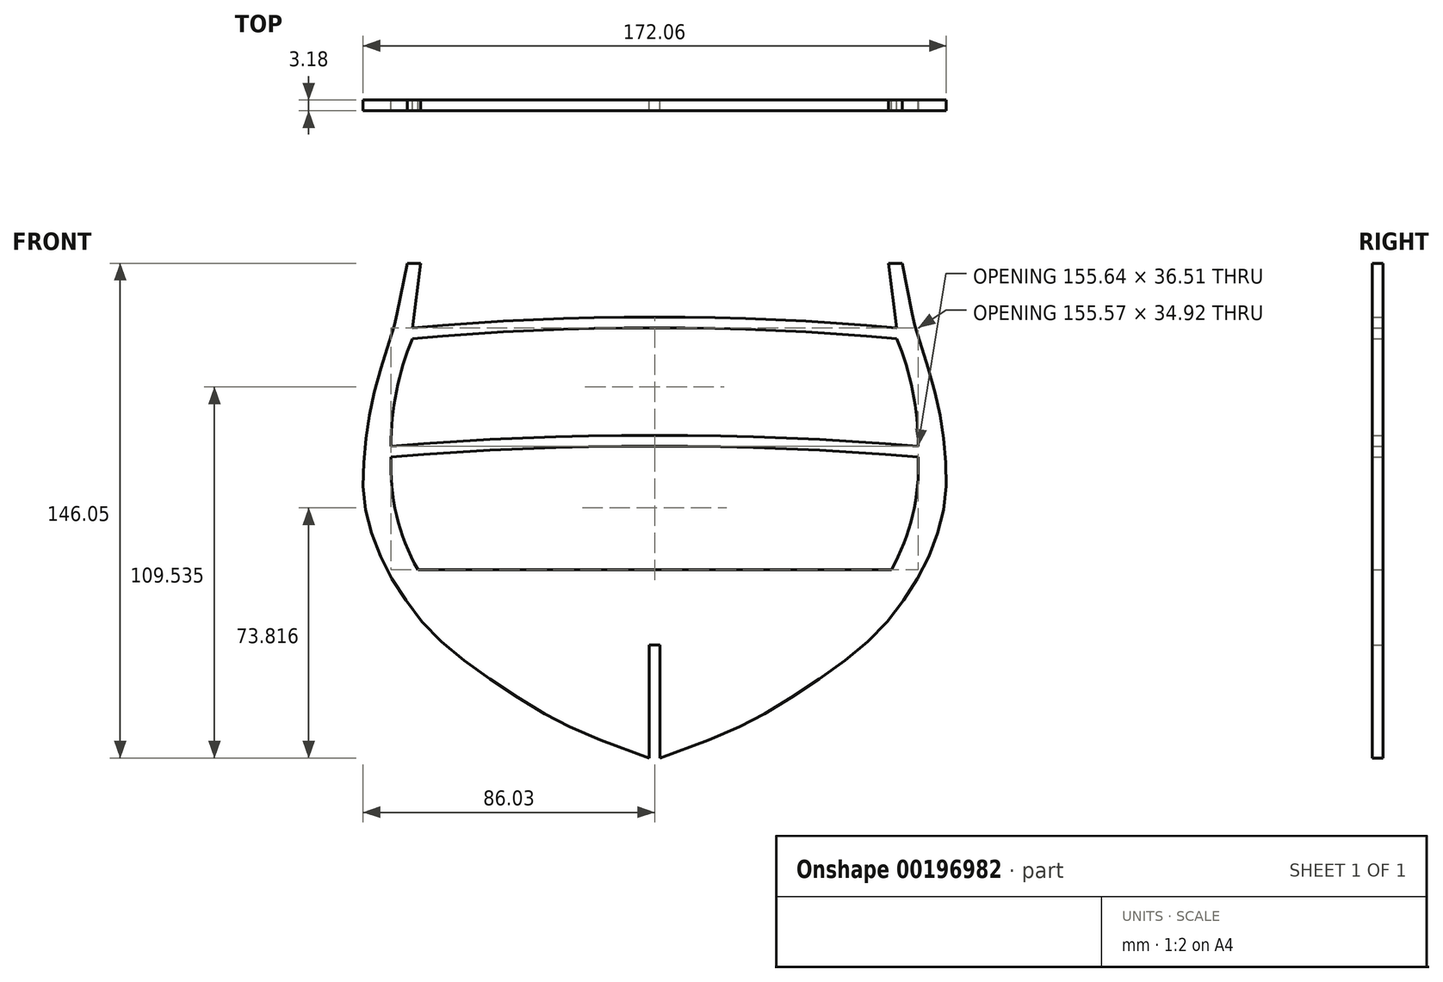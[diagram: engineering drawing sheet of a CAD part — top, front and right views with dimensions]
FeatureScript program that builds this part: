
annotation { "Feature Type Name" : "Feature", "Feature Type Description" : "" }
export const myFeature = defineFeature(function(context is Context, id is Id, definition is map)
    precondition{}
    {
        {
            var Q0;
            Q0=qCreatedBy(makeId("Front.planeOp"),FACE);
            var sketch = newSketch(context, id + "F0", { "sketchPlane" : qUnion([Q0])});
            skLineSegment(sketch, "E0", {"start": v(0, 0) * mm, "end": v(0, -22.22) * mm, "construction": true});
            skLineSegment(sketch, "E1", {"start": v(0, -22.22) * mm, "end": v(1.59, -22.22) * mm});
            skLineSegment(sketch, "E2", {"start": v(1.59, -22.22) * mm, "end": v(1.59, -55.56) * mm});
            skLineSegment(sketch, "E3", {"start": v(1.59, -55.56) * mm, "end": v(-1.59, -55.56) * mm, "construction": true});
            skLineSegment(sketch, "E4", {"start": v(-1.59, -55.56) * mm, "end": v(-1.59, -22.22) * mm});
            skLineSegment(sketch, "E5", {"start": v(-1.59, -22.22) * mm, "end": v(0, -22.22) * mm});
            skLineSegment(sketch, "E6", {"start": v(0, 0) * mm, "end": v(0, 33.34) * mm, "construction": true});
            skLineSegment(sketch, "E7", {"start": v(0, 33.34) * mm, "end": v(0, 36.51) * mm, "construction": true});
            skLineSegment(sketch, "E8", {"start": v(0, 36.51) * mm, "end": v(0, 68.26) * mm, "construction": true});
            skLineSegment(sketch, "E9", {"start": v(0, 68.26) * mm, "end": v(0, 71.44) * mm, "construction": true});
            skLineSegment(sketch, "E10", {"start": v(-71.44, 68.26) * mm, "end": v(0, 68.26) * mm, "construction": true});
            skLineSegment(sketch, "E11", {"start": v(0, 68.26) * mm, "end": v(71.44, 68.26) * mm, "construction": true});
            skLineSegment(sketch, "E12", {"start": v(0, 33.34) * mm, "end": v(77.79, 33.34) * mm, "construction": true});
            skLineSegment(sketch, "E13", {"start": v(0, 33.34) * mm, "end": v(-77.79, 33.34) * mm, "construction": true});
            skLineSegment(sketch, "E14", {"start": v(0, 0) * mm, "end": v(69.85, 0) * mm});
            skLineSegment(sketch, "E15", {"start": v(0, 0) * mm, "end": v(-69.85, 0) * mm});
            skArc(sketch, "E16", {"start": v(-77.79, 33.34) * mm, "mid": v(-76.14, 16.12) * mm, "end": v(-69.85, 0) * mm});
            skArc(sketch, "E17", {"start": v(69.85, 0) * mm, "mid": v(76.14, 16.12) * mm, "end": v(77.79, 33.34) * mm});
            skArc(sketch, "E18", {"start": v(77.79, 33.34) * mm, "mid": v(0, 36.51) * mm, "end": v(-77.79, 33.34) * mm});
            skLineSegment(sketch, "E19", {"start": v(-77.79, 36.51) * mm, "end": v(0, 36.51) * mm, "construction": true});
            skLineSegment(sketch, "E20", {"start": v(0, 36.51) * mm, "end": v(77.79, 36.51) * mm, "construction": true});
            skLineSegment(sketch, "E21", {"start": v(0, 71.44) * mm, "end": v(-71.44, 71.44) * mm, "construction": true});
            skLineSegment(sketch, "E22", {"start": v(0, 71.44) * mm, "end": v(71.44, 71.44) * mm, "construction": true});
            skArc(sketch, "E23", {"start": v(71.44, 71.44) * mm, "mid": v(0, 74.61) * mm, "end": v(-71.44, 71.44) * mm});
            skArc(sketch, "E24", {"start": v(71.44, 68.26) * mm, "mid": v(0, 71.44) * mm, "end": v(-71.44, 68.26) * mm});
            skArc(sketch, "E25", {"start": v(77.79, 36.51) * mm, "mid": v(0, 39.69) * mm, "end": v(-77.79, 36.51) * mm});
            skPoint(sketch, "E26", {"position": v(0, 39.69) * mm});
            skPoint(sketch, "E27", {"position": v(0, 71.44) * mm});
            skPoint(sketch, "E28", {"position": v(0, 74.61) * mm});
            skPoint(sketch, "E29", {"position": v(0, 36.51) * mm});
            skLineSegment(sketch, "E30", {"start": v(-77.79, 33.34) * mm, "end": v(-69.85, 0) * mm, "construction": true});
            skPoint(sketch, "E31", {"position": v(-73.82, 16.67) * mm});
            skPoint(sketch, "E32", {"position": v(-76.14, 16.12) * mm});
            skArc(sketch, "E33", {"start": v(-71.44, 68.26) * mm, "mid": v(-76.17, 52.7) * mm, "end": v(-77.79, 36.51) * mm});
            skArc(sketch, "E34", {"start": v(77.79, 36.51) * mm, "mid": v(76.17, 52.7) * mm, "end": v(71.44, 68.26) * mm});
            skLineSegment(sketch, "E35", {"start": v(-71.44, 68.26) * mm, "end": v(-77.79, 36.51) * mm, "construction": true});
            skPoint(sketch, "E36", {"position": v(-76.17, 52.7) * mm});
            skFitSpline(sketch, "E37", {"points": [v(1.59, -55.56) * mm, v(31.75, -42.86) * mm, v(51.6, -30.16) * mm, v(66.68, -17.46) * mm, v(76.2, -4.76) * mm, v(82.55, 7.94) * mm, v(85.73, 20.64) * mm, v(85.73, 33.34) * mm, v(84.14, 46.04) * mm, v(80.96, 58.74) * mm, v(77, 71.44) * mm, v(73.03, 90.49) * mm], "startDerivative": vector(413.95, 150.53) * mm, "endDerivative": vector(-122, 585.64) * mm});
            skLineSegment(sketch, "E38", {"start": v(73.03, 90.49) * mm, "end": v(69.06, 90.49) * mm});
            skLineSegment(sketch, "E39", {"start": v(69.06, 90.49) * mm, "end": v(71.44, 71.44) * mm});
            skFitSpline(sketch, "E40.MirrorCS", {"points": [v(-1.59, -55.56) * mm, v(-31.75, -42.86) * mm, v(-51.6, -30.16) * mm, v(-66.68, -17.46) * mm, v(-76.2, -4.76) * mm, v(-82.55, 7.94) * mm, v(-85.73, 20.64) * mm, v(-85.73, 33.34) * mm, v(-84.14, 46.04) * mm, v(-80.96, 58.74) * mm, v(-77, 71.44) * mm, v(-73.03, 90.49) * mm], "startDerivative": vector(-413.95, 150.53) * mm, "endDerivative": vector(122, 585.64) * mm});
            skLineSegment(sketch, "E41.MirrorCS", {"start": v(-69.06, 90.49) * mm, "end": v(-71.44, 71.44) * mm});
            skLineSegment(sketch, "E42.MirrorCS", {"start": v(-73.03, 90.49) * mm, "end": v(-69.06, 90.49) * mm});
            skSolve(sketch);
        }
        {
            var Q0;
            Q0 = qSketchRegion(id + "F0", true);
            extrude(context, id + "F1", {"entities" : qUnion([Q0]), "endBound" : BoundingType.SYMMETRIC, "depth" : 3.17 * mm});
        }
    });
